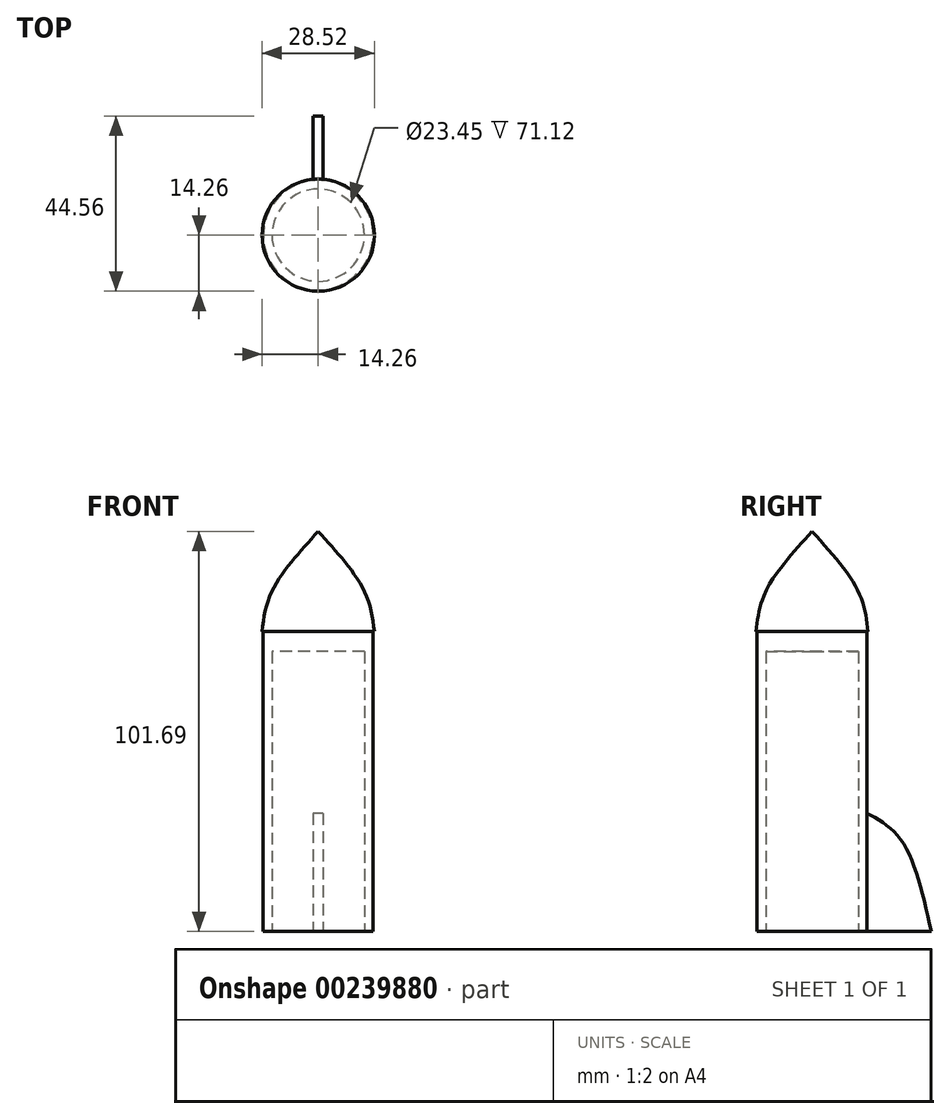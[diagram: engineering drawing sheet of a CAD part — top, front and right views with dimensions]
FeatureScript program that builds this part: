
annotation { "Feature Type Name" : "Feature", "Feature Type Description" : "" }
export const myFeature = defineFeature(function(context is Context, id is Id, definition is map)
    precondition{}
    {
        {
            var Q0;
            Q0=qCreatedBy(makeId("Top.planeOp"),FACE);
            var sketch = newSketch(context, id + "F0", { "sketchPlane" : qUnion([Q0])});
            skCircle(sketch, "E0", {"center": v(0, 0) * mm, "radius": 13.96 * mm});
            skSolve(sketch);
        }
        {
            var Q0;
            Q0 = qSketchRegion(id + "F0", true);
            extrude(context, id + "F1", {"entities" : qUnion([Q0]), "depth" : 76.2 * mm});
        }
        {
            var Q0;
            Q0=qCreatedBy(makeId("Top.planeOp"),FACE);
            var sketch = newSketch(context, id + "F2", { "sketchPlane" : qUnion([Q0])});
            skCircle(sketch, "E1", {"center": v(0, 0) * mm, "radius": 11.73 * mm});
            skSolve(sketch);
        }
        {
            var Q0;
            Q0 = qSketchRegion(id + "F2", true);
            extrude(context, id + "F3", {"entities" : qUnion([Q0]), "operationType" : NewBodyOperationType.REMOVE, "depth" : 71.12 * mm});
        }
        {
            var Q0;
            Q0=qCreatedBy(makeId("Right.planeOp"),FACE);
            var sketch = newSketch(context, id + "F4", { "sketchPlane" : qUnion([Q0])});
            skLineSegment(sketch, "E2", {"start": v(0, 76.3) * mm, "end": v(0, 101.69) * mm});
            skLineSegment(sketch, "E3", {"start": v(0, 76.3) * mm, "end": v(14.26, 76.3) * mm});
            skFitSpline(sketch, "E4", {"points": [v(14.26, 76.3) * mm, v(11.7, 86.57) * mm, v(0, 101.69) * mm], "startDerivative": vector(-2.95, 23.57) * mm, "endDerivative": vector(-24.52, 27.03) * mm});
            skSolve(sketch);
        }
        {
            var Q0;
            Q0=makeQuery(id+"F4.imprint","IMPRINT",FACE,{"disambiguationData":[TD([[makeQuery(id+"F4.imprint","IMPRINT",EDGE,{"derivedFrom":sQuery(id+"F4.wireOp",EDGE,"E2")}),-1.0]])]});
            var Q1;
            Q1=sQuery(id+"F4.wireOp",EDGE,"E2");
            revolve(context, id + "F5", {"entities" : qUnion([Q0]), "axis" : qUnion([Q1]), "revolveType" : RevolveType.FULL});
        }
        {
            var Q0;
            Q0=qCreatedBy(makeId("Right.planeOp"),FACE);
            var sketch = newSketch(context, id + "F6", { "sketchPlane" : qUnion([Q0])});
            skLineSegment(sketch, "E5", {"start": v(13.65, 30.22) * mm, "end": v(13.65, 0) * mm});
            skLineSegment(sketch, "E6", {"start": v(13.65, 0) * mm, "end": v(30.3, 0) * mm});
            skFitSpline(sketch, "E7", {"points": [v(13.65, 30.22) * mm, v(22.67, 23.23) * mm, v(30.3, 0) * mm], "startDerivative": vector(24.13, -12.78) * mm, "endDerivative": vector(10.05, -45.6) * mm});
            skSolve(sketch);
        }
        {
            var Q0;
            Q0=qCreatedBy(makeId("Right.planeOp"),FACE);
            var sketch = newSketch(context, id + "F7", { "sketchPlane" : qUnion([Q0])});
            skLineSegment(sketch, "E8", {"start": v(0, 0) * mm, "end": v(0, 69.84) * mm});
            skSolve(sketch);
        }
        {
            var Q0;
            Q0=makeQuery(id+"F6.imprint","IMPRINT",FACE,{"disambiguationData":[TD([[makeQuery(id+"F6.imprint","IMPRINT",EDGE,{"derivedFrom":sQuery(id+"F6.wireOp",EDGE,"E5")}),1.0]])]});
            extrude(context, id + "F8", {"entities" : qUnion([Q0]), "operationType" : NewBodyOperationType.ADD, "endBound" : BoundingType.SYMMETRIC, "depth" : 2.54 * mm});
        }
    });
